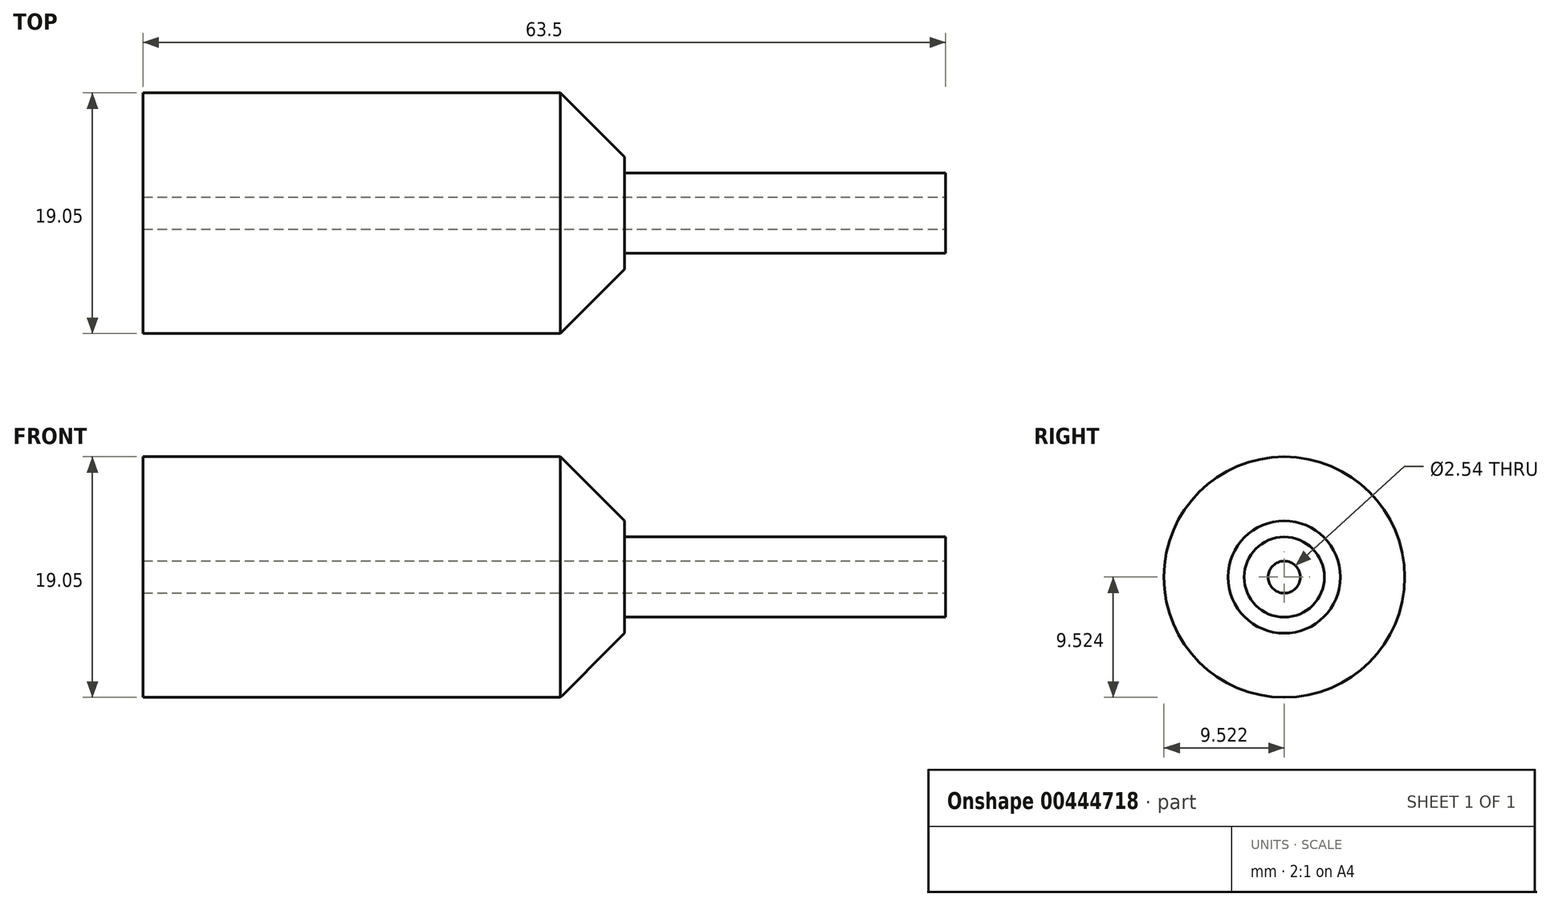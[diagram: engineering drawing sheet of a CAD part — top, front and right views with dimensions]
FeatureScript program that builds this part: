
annotation { "Feature Type Name" : "Feature", "Feature Type Description" : "" }
export const myFeature = defineFeature(function(context is Context, id is Id, definition is map)
    precondition{}
    {
        {
            var Q0;
            Q0=qCreatedBy(makeId("Right.planeOp"),FACE);
            var sketch = newSketch(context, id + "F0", { "sketchPlane" : qUnion([Q0])});
            skCircle(sketch, "E0", {"center": v(-128.23, 68.02) * mm, "radius": 9.53 * mm});
            skSolve(sketch);
        }
        {
            var Q0;
            Q0 = qSketchRegion(id + "F0", true);
            extrude(context, id + "F1", {"entities" : qUnion([Q0]), "depth" : 38.1 * mm});
        }
        {
            var Q0;
            Q0=makeQuery(id+"F1.opExtrude","CAP_FACE",FACE,{"disambiguationData":[OSD([sQuery(id+"F0.wireOp",EDGE,"E0")])],"isStart":false});
            chamfer(context, id + "F2", {"entities" : qUnion([Q0]), "width" : 5.08 * mm, "tangentPropagation" : true});
        }
        {
            var Q0;
            Q0=makeQuery(id+"F1.opExtrude","CAP_FACE",FACE,{"disambiguationData":[OSD([sQuery(id+"F0.wireOp",EDGE,"E0")])],"isStart":false});
            var sketch = newSketch(context, id + "F3", { "sketchPlane" : qUnion([Q0])});
            skCircle(sketch, "E1", {"center": v(-128.23, 68.02) * mm, "radius": 3.18 * mm});
            skSolve(sketch);
        }
        {
            var Q0;
            Q0 = qSketchRegion(id + "F3", true);
            extrude(context, id + "F4", {"entities" : qUnion([Q0]), "operationType" : NewBodyOperationType.ADD, "depth" : 25.4 * mm});
        }
        {
            var Q0;
            Q0=makeQuery(id+"F4.opExtrude","CAP_FACE",FACE,{"disambiguationData":[OSD([sQuery(id+"F3.wireOp",EDGE,"E1")])],"isStart":false});
            var sketch = newSketch(context, id + "F5", { "sketchPlane" : qUnion([Q0])});
            skCircle(sketch, "E2", {"center": v(-128.23, 68.02) * mm, "radius": 1.27 * mm});
            skSolve(sketch);
        }
        {
            var Q0;
            Q0 = qSketchRegion(id + "F5", true);
            extrude(context, id + "F6", {"entities" : qUnion([Q0]), "operationType" : NewBodyOperationType.REMOVE, "oppositeDirection" : true, "depth" : 189.48 * mm});
        }
    });
